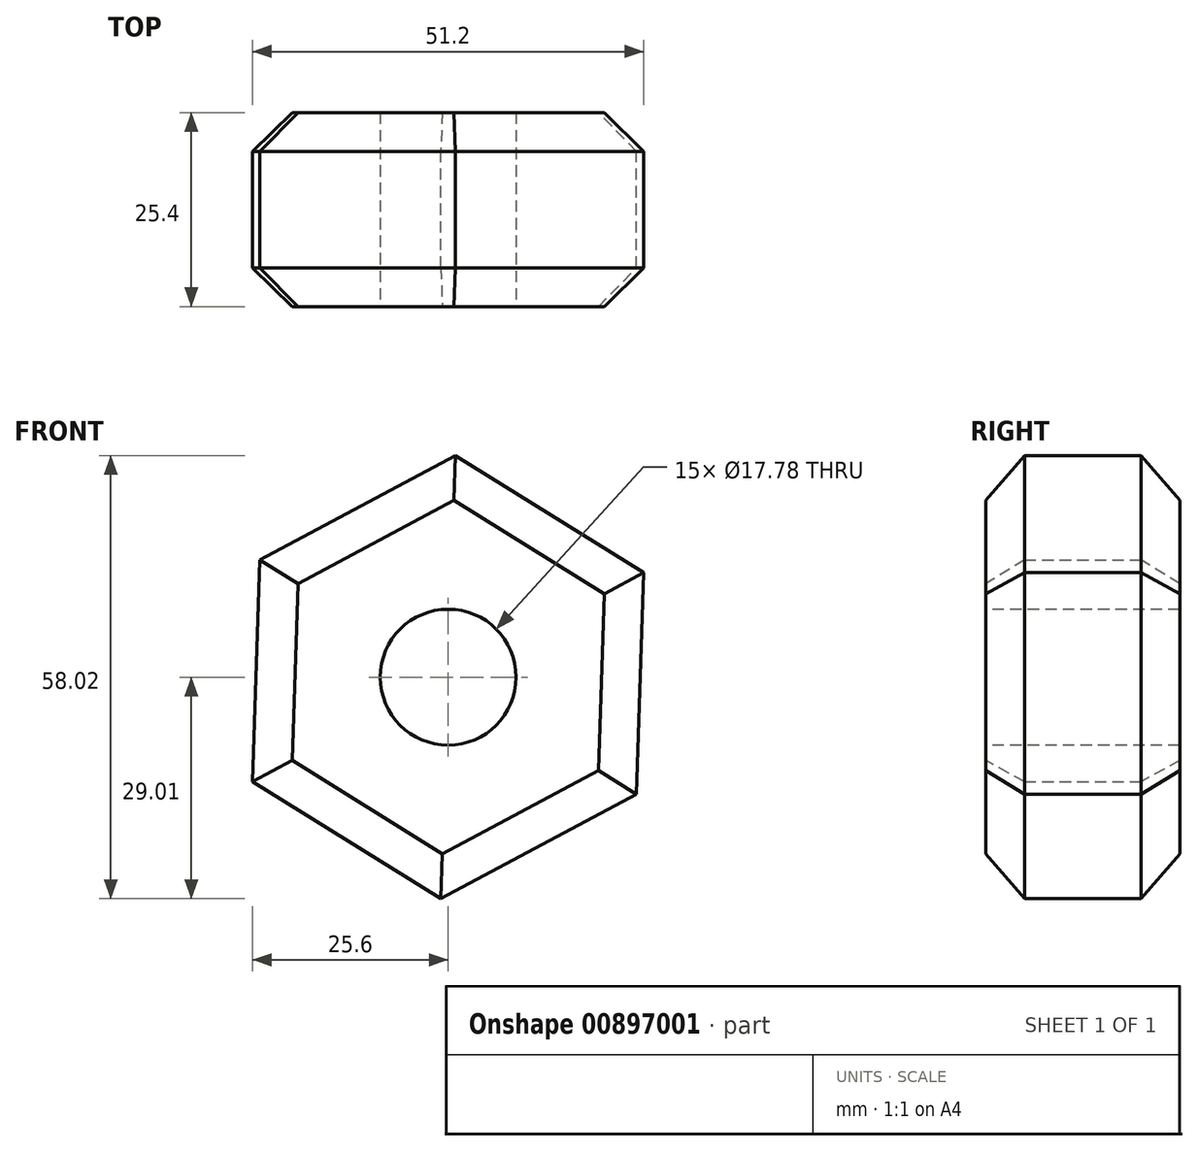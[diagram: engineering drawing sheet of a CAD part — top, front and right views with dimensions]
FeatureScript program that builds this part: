
annotation { "Feature Type Name" : "Feature", "Feature Type Description" : "" }
export const myFeature = defineFeature(function(context is Context, id is Id, definition is map)
    precondition{}
    {
        {
            var Q0;
            Q0=qCreatedBy(makeId("Front.planeOp"),FACE);
            var sketch = newSketch(context, id + "F0", { "sketchPlane" : qUnion([Q0])});
            skCircle(sketch, "E0.cCircle", {"center": v(0, 0) * mm, "radius": 25.13 * mm, "construction": true});
            skLineSegment(sketch, "E0.0", {"start": v(0.96, 29) * mm, "end": v(25.6, 13.67) * mm});
            skLineSegment(sketch, "E0.1", {"start": v(25.6, 13.67) * mm, "end": v(24.64, -15.33) * mm});
            skLineSegment(sketch, "E0.2", {"start": v(24.64, -15.33) * mm, "end": v(-0.96, -29) * mm});
            skLineSegment(sketch, "E0.3", {"start": v(-0.96, -29) * mm, "end": v(-25.6, -13.67) * mm});
            skLineSegment(sketch, "E0.4", {"start": v(-25.6, -13.67) * mm, "end": v(-24.64, 15.33) * mm});
            skLineSegment(sketch, "E0.5", {"start": v(-24.64, 15.33) * mm, "end": v(0.96, 29) * mm});
            skPoint(sketch, "E0.0.midPoint", {"position": v(13.28, 21.34) * mm});
            skSolve(sketch);
        }
        {
            var Q0;
            Q0=makeQuery(id+"F0.imprint","IMPRINT",FACE,{"disambiguationData":[TD([[makeQuery(id+"F0.imprint","IMPRINT",EDGE,{"derivedFrom":sQuery(id+"F0.wireOp",EDGE,"E0.0")}),-1.0]])]});
            extrude(context, id + "F1", {"entities" : qUnion([Q0]), "depth" : 25.4 * mm, "offsetDistance" : 25.4 * mm});
        }
        {
            var Q0;
            Q0=makeQuery(id+"F1.opExtrude","CAP_EDGE",EDGE,{"disambiguationData":[OSD([sQuery(id+"F0.wireOp",EDGE,"E0.0")])],"isStart":false});
            var Q1;
            Q1=makeQuery(id+"F1.opExtrude","CAP_EDGE",EDGE,{"disambiguationData":[OSD([sQuery(id+"F0.wireOp",EDGE,"E0.1")])],"isStart":false});
            var Q2;
            Q2=makeQuery(id+"F1.opExtrude","CAP_EDGE",EDGE,{"disambiguationData":[OSD([sQuery(id+"F0.wireOp",EDGE,"E0.2")])],"isStart":false});
            var Q3;
            Q3=makeQuery(id+"F1.opExtrude","CAP_EDGE",EDGE,{"disambiguationData":[OSD([sQuery(id+"F0.wireOp",EDGE,"E0.3")])],"isStart":false});
            var Q4;
            Q4=makeQuery(id+"F1.opExtrude","CAP_EDGE",EDGE,{"disambiguationData":[OSD([sQuery(id+"F0.wireOp",EDGE,"E0.4")])],"isStart":false});
            var Q5;
            Q5=makeQuery(id+"F1.opExtrude","CAP_EDGE",EDGE,{"disambiguationData":[OSD([sQuery(id+"F0.wireOp",EDGE,"E0.5")])],"isStart":false});
            chamfer(context, id + "F2", {"entities" : qUnion([Q0, Q1, Q2, Q3, Q4, Q5]), "width" : 5.08 * mm, "tangentPropagation" : true});
        }
        {
            var Q0;
            Q0=makeQuery(id+"F1.opExtrude","CAP_EDGE",EDGE,{"disambiguationData":[OSD([sQuery(id+"F0.wireOp",EDGE,"E0.1")])],"isStart":true});
            var Q1;
            Q1=makeQuery(id+"F1.opExtrude","CAP_EDGE",EDGE,{"disambiguationData":[OSD([sQuery(id+"F0.wireOp",EDGE,"E0.0")])],"isStart":true});
            var Q2;
            Q2=makeQuery(id+"F1.opExtrude","CAP_EDGE",EDGE,{"disambiguationData":[OSD([sQuery(id+"F0.wireOp",EDGE,"E0.2")])],"isStart":true});
            var Q3;
            Q3=makeQuery(id+"F1.opExtrude","CAP_EDGE",EDGE,{"disambiguationData":[OSD([sQuery(id+"F0.wireOp",EDGE,"E0.5")])],"isStart":true});
            var Q4;
            Q4=makeQuery(id+"F1.opExtrude","CAP_EDGE",EDGE,{"disambiguationData":[OSD([sQuery(id+"F0.wireOp",EDGE,"E0.4")])],"isStart":true});
            var Q5;
            Q5=makeQuery(id+"F1.opExtrude","CAP_EDGE",EDGE,{"disambiguationData":[OSD([sQuery(id+"F0.wireOp",EDGE,"E0.3")])],"isStart":true});
            chamfer(context, id + "F3", {"entities" : qUnion([Q0, Q1, Q2, Q3, Q4, Q5]), "width" : 5.08 * mm, "tangentPropagation" : true});
        }
        {
            var Q0;
            Q0=makeQuery(id+"F1.opExtrude","CAP_FACE",FACE,{"disambiguationData":[OSD([sQuery(id+"F0.wireOp",EDGE,"E0.0"),sQuery(id+"F0.wireOp",EDGE,"E0.1"),sQuery(id+"F0.wireOp",EDGE,"E0.2"),sQuery(id+"F0.wireOp",EDGE,"E0.3"),sQuery(id+"F0.wireOp",EDGE,"E0.4"),sQuery(id+"F0.wireOp",EDGE,"E0.5")])],"isStart":false});
            var sketch = newSketch(context, id + "F4", { "sketchPlane" : qUnion([Q0])});
            skCircle(sketch, "E1", {"center": v(0, 0) * mm, "radius": 9.19 * mm});
            skSolve(sketch);
        }
        {
            var Q0;
            Q0=sQuery(id+"F4.wireOp",VERTEX,"E1.center");
            var Q1;
            Q1=makeQuery(id+"F1.opExtrude","SWEPT_BODY",BODY,{"disambiguationData":[OSD([sQuery(id+"F0.wireOp",EDGE,"E0.0"),sQuery(id+"F0.wireOp",EDGE,"E0.1"),sQuery(id+"F0.wireOp",EDGE,"E0.2"),sQuery(id+"F0.wireOp",EDGE,"E0.3"),sQuery(id+"F0.wireOp",EDGE,"E0.4"),sQuery(id+"F0.wireOp",EDGE,"E0.5")])]});
            hole(context, id + "F5", {"style" : HoleStyle.SIMPLE, "endStyle" : HoleEndStyle.THROUGH, "holeDiameter" : 17.78 * mm, "majorDiameter" : 6.35 * mm, "isTappedThrough" : true, "tappedDepth" : 12.7 * mm, "tapClearance" : 3, "locations" : qUnion([Q0]), "scope" : qUnion([Q1])});
        }
    });
